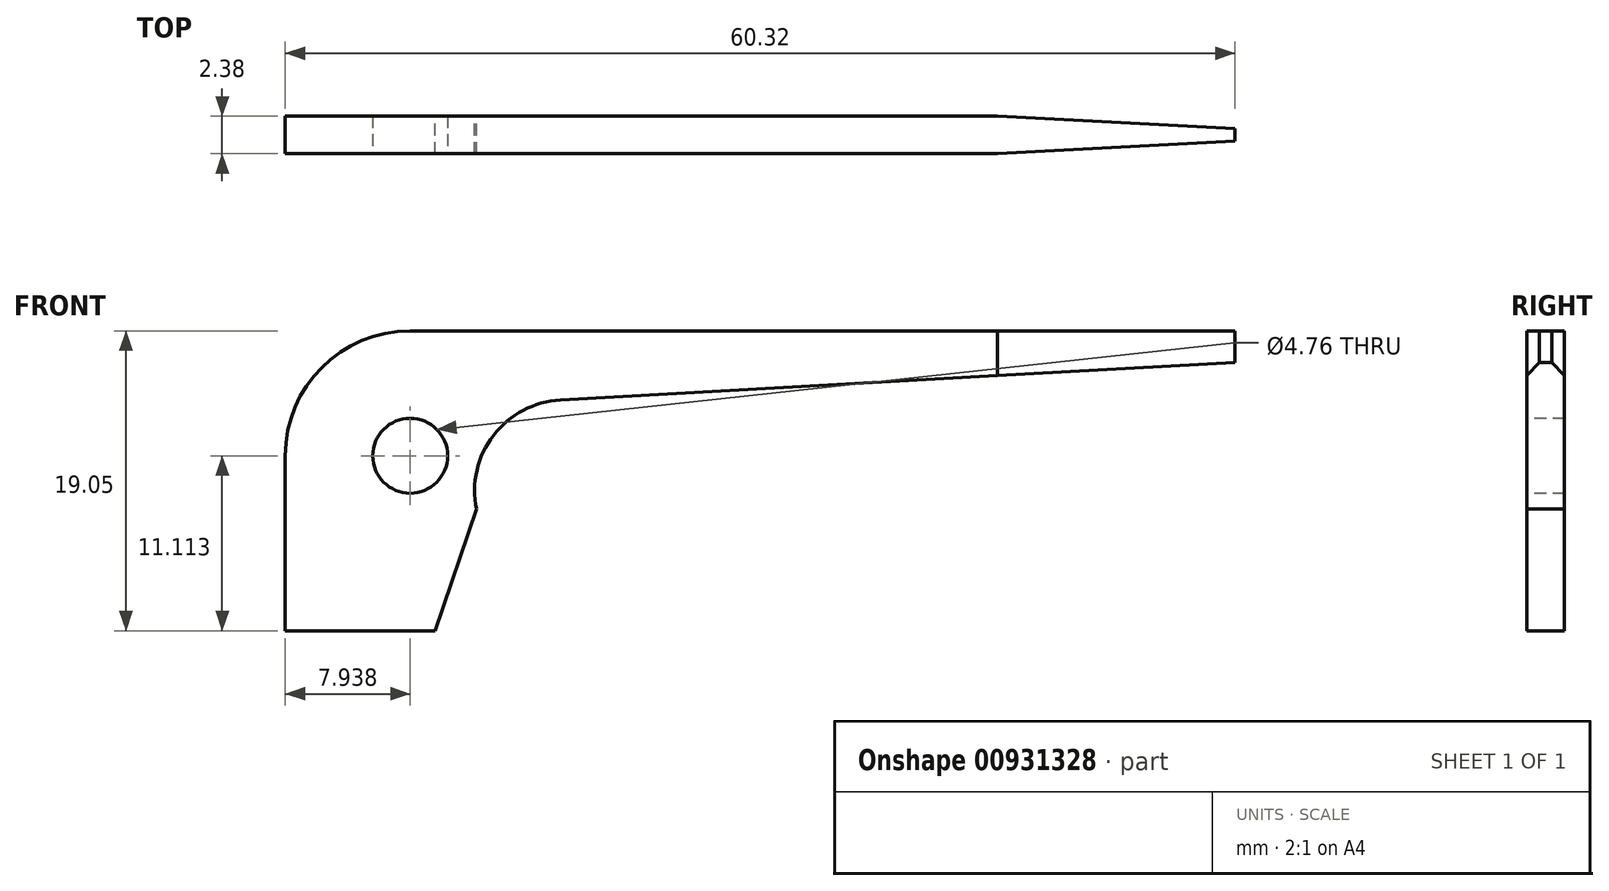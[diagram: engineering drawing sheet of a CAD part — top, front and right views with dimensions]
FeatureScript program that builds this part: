
annotation { "Feature Type Name" : "Feature", "Feature Type Description" : "" }
export const myFeature = defineFeature(function(context is Context, id is Id, definition is map)
    precondition{}
    {
        {
            var Q0;
            Q0=qCreatedBy(makeId("Front.planeOp"),FACE);
            var sketch = newSketch(context, id + "F0", { "sketchPlane" : qUnion([Q0])});
            skLineSegment(sketch, "E0.top", {"start": v(7.94, 19.05) * mm, "end": v(60.33, 19.05) * mm});
            skLineSegment(sketch, "E0.left", {"start": v(0, 0) * mm, "end": v(0, 11.11) * mm});
            skLineSegment(sketch, "E1", {"start": v(9.53, 0) * mm, "end": v(12.14, 7.72) * mm});
            skLineSegment(sketch, "E2", {"start": v(60.33, 17.05) * mm, "end": v(17.48, 14.66) * mm});
            skLineSegment(sketch, "E3", {"start": v(0, 0) * mm, "end": v(9.53, 0) * mm});
            skLineSegment(sketch, "E4", {"start": v(60.33, 19.05) * mm, "end": v(60.33, 17.05) * mm});
            skPoint(sketch, "E5.visualSharp", {"position": v(0, 19.05) * mm});
            skArc(sketch, "E5.filletArc", {"start": v(7.94, 19.05) * mm, "mid": v(2.32, 16.73) * mm, "end": v(0, 11.11) * mm});
            skArc(sketch, "E6", {"start": v(17.48, 14.66) * mm, "mid": v(13.22, 12.41) * mm, "end": v(12.14, 7.72) * mm});
            skSolve(sketch);
        }
        {
            var Q0;
            Q0=makeQuery(id+"F0.imprint","IMPRINT",FACE,{"disambiguationData":[TD([[makeQuery(id+"F0.imprint","IMPRINT",EDGE,{"derivedFrom":sQuery(id+"F0.wireOp",EDGE,"E0.top")}),-1.0]])]});
            extrude(context, id + "F1", {"entities" : qUnion([Q0]), "depth" : 2.38 * mm, "offsetDistance" : 25.4 * mm});
        }
        {
            var Q0;
            Q0=makeQuery(id+"F1.opExtrude","CAP_FACE",FACE,{"disambiguationData":[OSD([sQuery(id+"F0.wireOp",EDGE,"E0.top"),sQuery(id+"F0.wireOp",EDGE,"E0.left"),sQuery(id+"F0.wireOp",EDGE,"E1"),sQuery(id+"F0.wireOp",EDGE,"E2"),sQuery(id+"F0.wireOp",EDGE,"E3"),sQuery(id+"F0.wireOp",EDGE,"E4"),sQuery(id+"F0.wireOp",EDGE,"E5.filletArc"),sQuery(id+"F0.wireOp",EDGE,"E6")])],"isStart":false});
            var sketch = newSketch(context, id + "F2", { "sketchPlane" : qUnion([Q0])});
            skCircle(sketch, "E7", {"center": v(7.94, 11.11) * mm, "radius": 2.38 * mm});
            skSolve(sketch);
        }
        {
            var Q0;
            Q0=makeQuery(id+"F2.imprint","IMPRINT",FACE,{"disambiguationData":[TD([[makeQuery(id+"F2.imprint","IMPRINT",EDGE,{"derivedFrom":sQuery(id+"F2.wireOp",EDGE,"E7")}),1.0]])]});
            extrude(context, id + "F3", {"entities" : qUnion([Q0]), "operationType" : NewBodyOperationType.REMOVE, "oppositeDirection" : true, "depth" : 25.4 * mm, "offsetDistance" : 25.4 * mm});
        }
        {
            var Q0;
            Q0=makeQuery(id+"F1.opExtrude","SWEPT_FACE",FACE,{"disambiguationData":[OSD([sQuery(id+"F0.wireOp",EDGE,"E0.top")])]});
            var sketch = newSketch(context, id + "F4", { "sketchPlane" : qUnion([Q0])});
            skLineSegment(sketch, "E8", {"start": v(45.24, 0) * mm, "end": v(60.33, -0.8) * mm});
            skLineSegment(sketch, "E9.MirrorCS", {"start": v(45.24, -2.38) * mm, "end": v(60.33, -1.59) * mm});
            skSolve(sketch);
        }
        {
            var Q0;
            {var subQ0=sQuery(id+"F4.wireOp",EDGE,"E8");Q0=makeQuery(id+"F4.imprint","IMPRINT",FACE,{"disambiguationData":[TD([[makeQuery(id+"F4.imprint","IMPRINT",EDGE,{"derivedFrom":subQ0}),1.0]])]});}
            var Q1;
            {var subQ0=sQuery(id+"F4.wireOp",EDGE,"E9.MirrorCS");Q1=makeQuery(id+"F4.imprint","IMPRINT",FACE,{"disambiguationData":[TD([[makeQuery(id+"F4.imprint","IMPRINT",EDGE,{"derivedFrom":subQ0}),-1.0]])]});}
            extrude(context, id + "F5", {"entities" : qUnion([Q0, Q1]), "operationType" : NewBodyOperationType.REMOVE, "oppositeDirection" : true, "depth" : 25.4 * mm, "offsetDistance" : 25.4 * mm});
        }
    });
